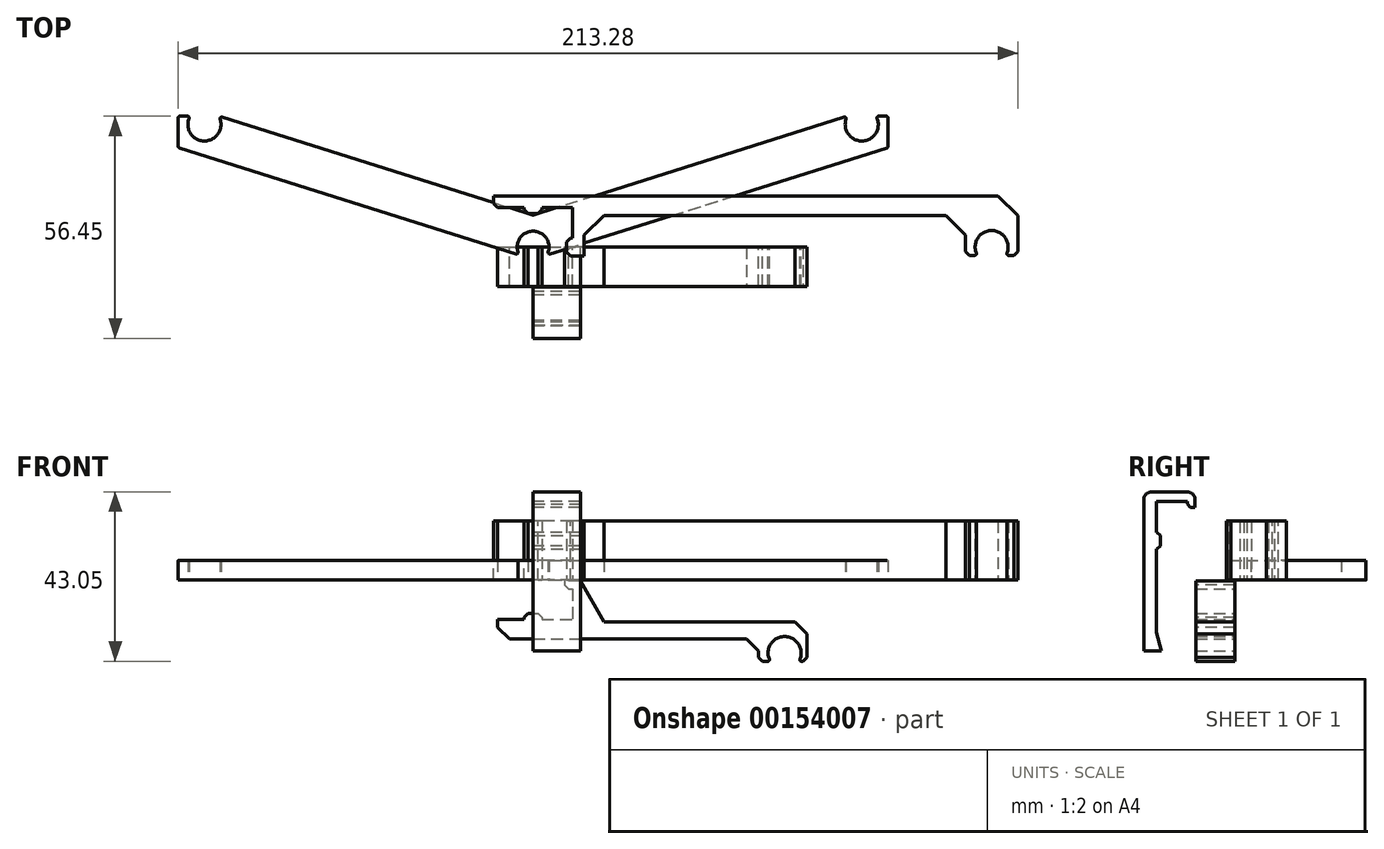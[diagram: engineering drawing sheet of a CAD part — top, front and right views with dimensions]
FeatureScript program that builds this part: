
annotation { "Feature Type Name" : "Feature", "Feature Type Description" : "" }
export const myFeature = defineFeature(function(context is Context, id is Id, definition is map)
    precondition{}
    {
        {
            var Q0;
            Q0=qCreatedBy(makeId("Front.planeOp"),FACE);
            var sketch = newSketch(context, id + "F0", { "sketchPlane" : qUnion([Q0])});
            skLineSegment(sketch, "E0.bottom", {"start": v(9, 10) * mm, "end": v(-9, 10) * mm});
            skLineSegment(sketch, "E0.top", {"start": v(9, -10) * mm, "end": v(-9, -10) * mm});
            skLineSegment(sketch, "E0.left", {"start": v(10, 9) * mm, "end": v(10, -9) * mm});
            skLineSegment(sketch, "E0.right", {"start": v(-10, 9) * mm, "end": v(-10, -9) * mm});
            skPoint(sketch, "E0.middle", {"position": v(0, 0) * mm});
            skPoint(sketch, "E1.visualSharp", {"position": v(10, 10) * mm});
            skArc(sketch, "E1.filletArc", {"start": v(10, 9) * mm, "mid": v(9.7, 9.7) * mm, "end": v(9, 10) * mm});
            skPoint(sketch, "E2.visualSharp", {"position": v(10, -10) * mm});
            skArc(sketch, "E2.filletArc", {"start": v(9, -10) * mm, "mid": v(9.7, -9.7) * mm, "end": v(10, -9) * mm});
            skPoint(sketch, "E3.visualSharp", {"position": v(-10, 10) * mm});
            skArc(sketch, "E3.filletArc", {"start": v(-9, 10) * mm, "mid": v(-9.7, 9.7) * mm, "end": v(-10, 9) * mm});
            skPoint(sketch, "E4.visualSharp", {"position": v(-10, -10) * mm});
            skArc(sketch, "E4.filletArc", {"start": v(-10, -9) * mm, "mid": v(-9.7, -9.7) * mm, "end": v(-9, -10) * mm});
            skLineSegment(sketch, "E5", {"start": v(10, 2.25) * mm, "end": v(8.5, 2.25) * mm});
            skLineSegment(sketch, "E6", {"start": v(8.5, 2.25) * mm, "end": v(8.5, 3.75) * mm});
            skLineSegment(sketch, "E7", {"start": v(8.5, 3.75) * mm, "end": v(4.45, 3.75) * mm});
            skLineSegment(sketch, "E8", {"start": v(10, -2.25) * mm, "end": v(8.5, -2.25) * mm});
            skLineSegment(sketch, "E9", {"start": v(8.5, -2.25) * mm, "end": v(8.5, -3.75) * mm});
            skLineSegment(sketch, "E10", {"start": v(8.5, -3.75) * mm, "end": v(4.45, -3.75) * mm});
            skArc(sketch, "E11", {"start": v(4.45, 3.75) * mm, "mid": v(3.3, 0) * mm, "end": v(4.45, -3.75) * mm});
            skLineSegment(sketch, "E12.1.0", {"start": v(-3.75, 8.5) * mm, "end": v(-3.75, 4.45) * mm});
            skArc(sketch, "E12.1.1", {"start": v(-3.75, 4.45) * mm, "mid": v(0, 3.3) * mm, "end": v(3.75, 4.45) * mm});
            skLineSegment(sketch, "E12.1.2", {"start": v(3.75, 8.5) * mm, "end": v(3.75, 4.45) * mm});
            skLineSegment(sketch, "E12.1.3", {"start": v(2.25, 8.5) * mm, "end": v(3.75, 8.5) * mm});
            skLineSegment(sketch, "E12.1.4", {"start": v(2.25, 10) * mm, "end": v(2.25, 8.5) * mm});
            skLineSegment(sketch, "E12.1.5", {"start": v(-2.25, 10) * mm, "end": v(-2.25, 8.5) * mm});
            skLineSegment(sketch, "E12.1.6", {"start": v(-2.25, 8.5) * mm, "end": v(-3.75, 8.5) * mm});
            skLineSegment(sketch, "E12.2.0", {"start": v(-8.5, -3.75) * mm, "end": v(-4.45, -3.75) * mm});
            skArc(sketch, "E12.2.1", {"start": v(-4.45, -3.75) * mm, "mid": v(-3.3, 0) * mm, "end": v(-4.45, 3.75) * mm});
            skLineSegment(sketch, "E12.2.2", {"start": v(-8.5, 3.75) * mm, "end": v(-4.45, 3.75) * mm});
            skLineSegment(sketch, "E12.2.3", {"start": v(-8.5, 2.25) * mm, "end": v(-8.5, 3.75) * mm});
            skLineSegment(sketch, "E12.2.4", {"start": v(-10, 2.25) * mm, "end": v(-8.5, 2.25) * mm});
            skLineSegment(sketch, "E12.2.5", {"start": v(-10, -2.25) * mm, "end": v(-8.5, -2.25) * mm});
            skLineSegment(sketch, "E12.2.6", {"start": v(-8.5, -2.25) * mm, "end": v(-8.5, -3.75) * mm});
            skLineSegment(sketch, "E12.3.0", {"start": v(3.75, -8.5) * mm, "end": v(3.75, -4.45) * mm});
            skArc(sketch, "E12.3.1", {"start": v(3.75, -4.45) * mm, "mid": v(0, -3.3) * mm, "end": v(-3.75, -4.45) * mm});
            skLineSegment(sketch, "E12.3.2", {"start": v(-3.75, -8.5) * mm, "end": v(-3.75, -4.45) * mm});
            skLineSegment(sketch, "E12.3.3", {"start": v(-2.25, -8.5) * mm, "end": v(-3.75, -8.5) * mm});
            skLineSegment(sketch, "E12.3.4", {"start": v(-2.25, -10) * mm, "end": v(-2.25, -8.5) * mm});
            skLineSegment(sketch, "E12.3.5", {"start": v(2.25, -10) * mm, "end": v(2.25, -8.5) * mm});
            skLineSegment(sketch, "E12.3.6", {"start": v(2.25, -8.5) * mm, "end": v(3.75, -8.5) * mm});
            skSolve(sketch);
        }
        {
            var Q0;
            Q0=qCreatedBy(makeId("Front.planeOp"),FACE);
            var sketch = newSketch(context, id + "F1", { "sketchPlane" : qUnion([Q0])});
            skLineSegment(sketch, "E13.0", {"start": v(10, -2.25) * mm, "end": v(8.5, -2.25) * mm, "construction": true});
            skLineSegment(sketch, "E14.0", {"start": v(10, 9) * mm, "end": v(10, -9) * mm, "construction": true});
            skLineSegment(sketch, "E15.0", {"start": v(9, -10) * mm, "end": v(-9, -10) * mm, "construction": true});
            skLineSegment(sketch, "E16.0", {"start": v(2.25, -10) * mm, "end": v(2.25, -8.5) * mm, "construction": true});
            skLineSegment(sketch, "E17.0", {"start": v(-2.25, -10) * mm, "end": v(-2.25, -8.5) * mm, "construction": true});
            skLineSegment(sketch, "E18", {"start": v(8, -2.25) * mm, "end": v(10, -2.25) * mm});
            skLineSegment(sketch, "E19", {"start": v(10, -2.25) * mm, "end": v(10, -10) * mm});
            skCircle(sketch, "E20", {"center": v(63.9, -18.55) * mm, "radius": 4.2 * mm});
            skLineSegment(sketch, "E21", {"start": v(-9, -10) * mm, "end": v(-9, -20.65) * mm});
            skLineSegment(sketch, "E22", {"start": v(-9, -20.65) * mm, "end": v(60.26, -20.65) * mm});
            skLineSegment(sketch, "E23", {"start": v(67.54, -20.65) * mm, "end": v(69.54, -20.65) * mm});
            skLineSegment(sketch, "E24", {"start": v(69.54, -20.65) * mm, "end": v(69.54, -10.65) * mm});
            skLineSegment(sketch, "E25", {"start": v(69.54, -10.65) * mm, "end": v(18, -10.65) * mm});
            skLineSegment(sketch, "E26", {"start": v(18, -10.65) * mm, "end": v(12, -0.25) * mm});
            skLineSegment(sketch, "E27", {"start": v(12, -0.25) * mm, "end": v(8, -0.25) * mm});
            skLineSegment(sketch, "E28", {"start": v(8, -0.25) * mm, "end": v(8, -2.25) * mm});
            skLineSegment(sketch, "E29", {"start": v(-9, -15) * mm, "end": v(57.26, -15) * mm});
            skLineSegment(sketch, "E30", {"start": v(57.26, -15) * mm, "end": v(57.26, -20.65) * mm});
            skLineSegment(sketch, "E31", {"start": v(63.9, -18.55) * mm, "end": v(60.26, -20.65) * mm, "construction": true});
            skLineSegment(sketch, "E32", {"start": v(63.9, -18.55) * mm, "end": v(67.54, -20.65) * mm, "construction": true});
            skLineSegment(sketch, "E33", {"start": v(59.7, -18.55) * mm, "end": v(68.1, -18.55) * mm, "construction": true});
            skLineSegment(sketch, "E34", {"start": v(-9, -10) * mm, "end": v(-2.25, -10) * mm});
            skLineSegment(sketch, "E35", {"start": v(-2.25, -10) * mm, "end": v(-2.25, -8.5) * mm});
            skLineSegment(sketch, "E36", {"start": v(-2.25, -8.5) * mm, "end": v(2.25, -8.5) * mm});
            skLineSegment(sketch, "E37", {"start": v(2.25, -8.5) * mm, "end": v(2.25, -10) * mm});
            skLineSegment(sketch, "E38", {"start": v(2.25, -10) * mm, "end": v(10, -10) * mm});
            skSolve(sketch);
        }
        {
            var Q0;
            Q0=makeQuery(id+"F1.imprint","IMPRINT",FACE,{"disambiguationData":[TD([[makeQuery(id+"F1.imprint","IMPRINT",EDGE,{"derivedFrom":sQuery(id+"F1.wireOp",EDGE,"E18")}),1.0]])]});
            extrude(context, id + "F2", {"entities" : qUnion([Q0]), "depth" : 10 * mm});
        }
        {
            var Q0;
            Q0=makeQuery(id+"F2.opExtrude","SWEPT_EDGE",EDGE,{"disambiguationData":[OSD([sQuery(id+"F1.wireOp",EDGE,"E35"),sQuery(id+"F1.wireOp",EDGE,"E36")])]});
            var Q1;
            Q1=makeQuery(id+"F2.opExtrude","SWEPT_EDGE",EDGE,{"disambiguationData":[OSD([sQuery(id+"F1.wireOp",EDGE,"E36"),sQuery(id+"F1.wireOp",EDGE,"E37")])]});
            var Q2;
            Q2=makeQuery(id+"F2.opExtrude","SWEPT_EDGE",EDGE,{"disambiguationData":[OSD([sQuery(id+"F1.wireOp",EDGE,"E18"),sQuery(id+"F1.wireOp",EDGE,"E28")])]});
            var Q3;
            Q3=makeQuery(id+"F2.opExtrude","SWEPT_EDGE",EDGE,{"disambiguationData":[OSD([sQuery(id+"F1.wireOp",EDGE,"E22"),sQuery(id+"F1.wireOp",EDGE,"E30")])]});
            var Q4;
            Q4=makeQuery(id+"F2.opExtrude","SWEPT_EDGE",EDGE,{"disambiguationData":[OSD([sQuery(id+"F1.wireOp",EDGE,"E23"),sQuery(id+"F1.wireOp",EDGE,"E24")])]});
            chamfer(context, id + "F3", {"entities" : qUnion([Q0, Q1, Q2, Q3, Q4]), "width" : 1 * mm, "tangentPropagation" : true});
        }
        {
            var Q0;
            Q0=makeQuery(id+"F2.opExtrude","SWEPT_EDGE",EDGE,{"disambiguationData":[OSD([sQuery(id+"F1.wireOp",EDGE,"E21"),sQuery(id+"F1.wireOp",EDGE,"E29")])]});
            var Q1;
            Q1=makeQuery(id+"F2.opExtrude","SWEPT_EDGE",EDGE,{"disambiguationData":[OSD([sQuery(id+"F1.wireOp",EDGE,"E29"),sQuery(id+"F1.wireOp",EDGE,"E30")])]});
            var Q2;
            Q2=makeQuery(id+"F2.opExtrude","SWEPT_EDGE",EDGE,{"disambiguationData":[OSD([sQuery(id+"F1.wireOp",EDGE,"E24"),sQuery(id+"F1.wireOp",EDGE,"E25")])]});
            chamfer(context, id + "F4", {"entities" : qUnion([Q0, Q1, Q2]), "width" : 3 * mm, "tangentPropagation" : true});
        }
        {
            var Q0;
            Q0=qCreatedBy(makeId("Top.planeOp"),FACE);
            var sketch = newSketch(context, id + "F5", { "sketchPlane" : qUnion([Q0])});
            skLineSegment(sketch, "E39.bottom", {"start": v(10, 10) * mm, "end": v(-10, 10) * mm, "construction": true});
            skLineSegment(sketch, "E39.top", {"start": v(10, -10) * mm, "end": v(-10, -10) * mm, "construction": true});
            skLineSegment(sketch, "E39.left", {"start": v(10, 10) * mm, "end": v(10, -10) * mm, "construction": true});
            skLineSegment(sketch, "E39.right", {"start": v(-10, 10) * mm, "end": v(-10, -10) * mm, "construction": true});
            skPoint(sketch, "E39.middle", {"position": v(0, 0) * mm});
            skCircle(sketch, "E40", {"center": v(116.5, 0) * mm, "radius": 4.2 * mm});
            skLineSegment(sketch, "E41", {"start": v(-10, 10) * mm, "end": v(-10, 13) * mm});
            skLineSegment(sketch, "E42", {"start": v(-10, 13) * mm, "end": v(123.14, 13) * mm});
            skLineSegment(sketch, "E43", {"start": v(123.14, 13) * mm, "end": v(123.14, -2.1) * mm});
            skLineSegment(sketch, "E44", {"start": v(123.14, -2.1) * mm, "end": v(120.14, -2.1) * mm});
            skLineSegment(sketch, "E45", {"start": v(112.86, -2.1) * mm, "end": v(109.86, -2.1) * mm});
            skLineSegment(sketch, "E46", {"start": v(109.86, -2.1) * mm, "end": v(109.86, 8) * mm});
            skLineSegment(sketch, "E47", {"start": v(109.86, 8) * mm, "end": v(13, 8) * mm});
            skLineSegment(sketch, "E48", {"start": v(13, 8) * mm, "end": v(13, -2.25) * mm});
            skLineSegment(sketch, "E49", {"start": v(13, -2.25) * mm, "end": v(10, -2.25) * mm});
            skLineSegment(sketch, "E50", {"start": v(10, -2.25) * mm, "end": v(8.5, -2.25) * mm});
            skLineSegment(sketch, "E51", {"start": v(8.5, -2.25) * mm, "end": v(8.5, 2.25) * mm});
            skLineSegment(sketch, "E52", {"start": v(8.5, 2.25) * mm, "end": v(10, 2.25) * mm});
            skLineSegment(sketch, "E53", {"start": v(10, 2.25) * mm, "end": v(10, 10) * mm});
            skLineSegment(sketch, "E54", {"start": v(10, 10) * mm, "end": v(2.25, 10) * mm});
            skLineSegment(sketch, "E55", {"start": v(2.25, 10) * mm, "end": v(2.25, 8.5) * mm});
            skLineSegment(sketch, "E56", {"start": v(2.25, 8.5) * mm, "end": v(-2.25, 8.5) * mm});
            skLineSegment(sketch, "E57", {"start": v(-2.25, 8.5) * mm, "end": v(-2.25, 10) * mm});
            skLineSegment(sketch, "E58", {"start": v(-2.25, 10) * mm, "end": v(-10, 10) * mm});
            skLineSegment(sketch, "E59", {"start": v(112.3, 0) * mm, "end": v(120.7, 0) * mm, "construction": true});
            skLineSegment(sketch, "E60", {"start": v(116.5, 0) * mm, "end": v(112.86, -2.1) * mm, "construction": true});
            skLineSegment(sketch, "E61", {"start": v(116.5, 0) * mm, "end": v(120.14, -2.1) * mm, "construction": true});
            skSolve(sketch);
        }
        {
            var Q0;
            Q0=makeQuery(id+"F5.imprint","IMPRINT",FACE,{"disambiguationData":[TD([[makeQuery(id+"F5.imprint","IMPRINT",EDGE,{"derivedFrom":sQuery(id+"F5.wireOp",EDGE,"E41")}),-1.0]])]});
            extrude(context, id + "F6", {"entities" : qUnion([Q0]), "depth" : 15 * mm});
        }
        {
            var Q0;
            Q0=makeQuery(id+"F6.opExtrude","SWEPT_EDGE",EDGE,{"disambiguationData":[OSD([sQuery(id+"F5.wireOp",EDGE,"E51"),sQuery(id+"F5.wireOp",EDGE,"E52")])]});
            var Q1;
            Q1=makeQuery(id+"F6.opExtrude","SWEPT_EDGE",EDGE,{"disambiguationData":[OSD([sQuery(id+"F5.wireOp",EDGE,"E50"),sQuery(id+"F5.wireOp",EDGE,"E51")])]});
            var Q2;
            Q2=makeQuery(id+"F6.opExtrude","SWEPT_EDGE",EDGE,{"disambiguationData":[OSD([sQuery(id+"F5.wireOp",EDGE,"E56"),sQuery(id+"F5.wireOp",EDGE,"E57")])]});
            var Q3;
            Q3=makeQuery(id+"F6.opExtrude","SWEPT_EDGE",EDGE,{"disambiguationData":[OSD([sQuery(id+"F5.wireOp",EDGE,"E55"),sQuery(id+"F5.wireOp",EDGE,"E56")])]});
            var Q4;
            Q4=makeQuery(id+"F6.opExtrude","SWEPT_EDGE",EDGE,{"disambiguationData":[OSD([sQuery(id+"F5.wireOp",EDGE,"E41"),sQuery(id+"F5.wireOp",EDGE,"E58")])]});
            var Q5;
            Q5=makeQuery(id+"F6.opExtrude","SWEPT_EDGE",EDGE,{"disambiguationData":[OSD([sQuery(id+"F5.wireOp",EDGE,"E45"),sQuery(id+"F5.wireOp",EDGE,"E46")])]});
            var Q6;
            Q6=makeQuery(id+"F6.opExtrude","SWEPT_EDGE",EDGE,{"disambiguationData":[OSD([sQuery(id+"F5.wireOp",EDGE,"E43"),sQuery(id+"F5.wireOp",EDGE,"E44")])]});
            chamfer(context, id + "F7", {"entities" : qUnion([Q0, Q1, Q2, Q3, Q4, Q5, Q6]), "width" : 1 * mm, "tangentPropagation" : true});
        }
        {
            var Q0;
            Q0=makeQuery(id+"F6.opExtrude","SWEPT_EDGE",EDGE,{"disambiguationData":[OSD([sQuery(id+"F5.wireOp",EDGE,"E42"),sQuery(id+"F5.wireOp",EDGE,"E43")])]});
            var Q1;
            Q1=makeQuery(id+"F6.opExtrude","SWEPT_EDGE",EDGE,{"disambiguationData":[OSD([sQuery(id+"F5.wireOp",EDGE,"E46"),sQuery(id+"F5.wireOp",EDGE,"E47")])]});
            var Q2;
            Q2=makeQuery(id+"F6.opExtrude","SWEPT_EDGE",EDGE,{"disambiguationData":[OSD([sQuery(id+"F5.wireOp",EDGE,"E47"),sQuery(id+"F5.wireOp",EDGE,"E48")])]});
            chamfer(context, id + "F8", {"entities" : qUnion([Q0, Q1, Q2]), "width" : 5 * mm, "tangentPropagation" : true});
        }
        {
            var Q0;
            Q0=makeQuery(id+"F2.opExtrude","SWEPT_EDGE",EDGE,{"disambiguationData":[OSD([sQuery(id+"F1.wireOp",EDGE,"E20"),sQuery(id+"F1.wireOp",EDGE,"E22")])]});
            var Q1;
            Q1=makeQuery(id+"F2.opExtrude","SWEPT_EDGE",EDGE,{"disambiguationData":[OSD([sQuery(id+"F1.wireOp",EDGE,"E20"),sQuery(id+"F1.wireOp",EDGE,"E23")])]});
            var Q2;
            Q2=makeQuery(id+"F6.opExtrude","SWEPT_EDGE",EDGE,{"disambiguationData":[OSD([sQuery(id+"F5.wireOp",EDGE,"E40"),sQuery(id+"F5.wireOp",EDGE,"E45")])]});
            var Q3;
            Q3=makeQuery(id+"F6.opExtrude","SWEPT_EDGE",EDGE,{"disambiguationData":[OSD([sQuery(id+"F5.wireOp",EDGE,"E40"),sQuery(id+"F5.wireOp",EDGE,"E44")])]});
            fillet(context, id + "F9", {"entities" : qUnion([Q0, Q1, Q2, Q3]), "radius" : 0.4 * mm, "tangentPropagation" : true, "allowEdgeOverflow" : false});
        }
        {
            var Q0;
            Q0=qCreatedBy(makeId("Top.planeOp"),FACE);
            var sketch = newSketch(context, id + "F10", { "sketchPlane" : qUnion([Q0])});
            skCircle(sketch, "E62", {"center": v(0, 0) * mm, "radius": 4.05 * mm});
            skCircle(sketch, "E63", {"center": v(-83.5, 31.15) * mm, "radius": 4.2 * mm});
            skLineSegment(sketch, "E64", {"start": v(0, 0) * mm, "end": v(0, 66.48) * mm, "construction": true});
            skCircle(sketch, "E65.MirrorC", {"center": v(83.5, 31.15) * mm, "radius": 4.2 * mm});
            skLineSegment(sketch, "E66", {"start": v(-79.3, 31.15) * mm, "end": v(-87.7, 31.15) * mm, "construction": true});
            skLineSegment(sketch, "E67", {"start": v(-4.05, 0) * mm, "end": v(4.05, 0) * mm, "construction": true});
            skLineSegment(sketch, "E68", {"start": v(-83.5, 31.15) * mm, "end": v(-87.14, 33.25) * mm, "construction": true});
            skLineSegment(sketch, "E69", {"start": v(-83.5, 31.15) * mm, "end": v(-79.86, 33.25) * mm, "construction": true});
            skLineSegment(sketch, "E70", {"start": v(0, 0) * mm, "end": v(-3.5, -2.02) * mm, "construction": true});
            skLineSegment(sketch, "E71", {"start": v(0, 0) * mm, "end": v(3.5, -2.02) * mm, "construction": true});
            skLineSegment(sketch, "E72", {"start": v(-87.14, 33.25) * mm, "end": v(-90.14, 33.25) * mm});
            skLineSegment(sketch, "E73", {"start": v(-90.14, 33.25) * mm, "end": v(-90.14, 25.25) * mm});
            skLineSegment(sketch, "E74", {"start": v(-90.14, 25.25) * mm, "end": v(-90.14, 25.25) * mm});
            skLineSegment(sketch, "E75", {"start": v(-3.5, -2.03) * mm, "end": v(-90.14, 25.25) * mm});
            skLineSegment(sketch, "E76", {"start": v(-79.86, 33.25) * mm, "end": v(0, 8.1) * mm});
            skLineSegment(sketch, "E77.MirrorCS", {"start": v(79.86, 33.25) * mm, "end": v(0, 8.1) * mm});
            skLineSegment(sketch, "E78.MirrorCS", {"start": v(3.5, -2.03) * mm, "end": v(90.14, 25.25) * mm});
            skLineSegment(sketch, "E79.MirrorCS", {"start": v(90.14, 33.25) * mm, "end": v(90.14, 25.25) * mm});
            skLineSegment(sketch, "E80.MirrorCS", {"start": v(83.5, 31.15) * mm, "end": v(79.86, 33.25) * mm, "construction": true});
            skLineSegment(sketch, "E81.MirrorCS", {"start": v(83.5, 31.15) * mm, "end": v(87.14, 33.25) * mm, "construction": true});
            skLineSegment(sketch, "E82.MirrorCS", {"start": v(87.14, 33.25) * mm, "end": v(90.14, 33.25) * mm});
            skSolve(sketch);
        }
        {
            var Q0;
            {var subQ5=sQuery(id+"F10.wireOp",EDGE,"E72");Q0=makeQuery(id+"F10.imprint","IMPRINT",FACE,{"disambiguationData":[TD([[makeQuery(id+"F10.imprint","IMPRINT",EDGE,{"derivedFrom":subQ5}),1.0]])]});}
            extrude(context, id + "F15", {"entities" : qUnion([Q0]), "depth" : 5 * mm});
        }
        {
            var Q0;
            Q0=makeQuery(id+"F15.opExtrude","SWEPT_EDGE",EDGE,{"disambiguationData":[OSD([sQuery(id+"F10.wireOp",EDGE,"E62"),sQuery(id+"F10.wireOp",EDGE,"E75")])]});
            var Q1;
            Q1=makeQuery(id+"F15.opExtrude","SWEPT_EDGE",EDGE,{"disambiguationData":[OSD([sQuery(id+"F10.wireOp",EDGE,"E62"),sQuery(id+"F10.wireOp",EDGE,"E78.MirrorCS")])]});
            var Q2;
            Q2=makeQuery(id+"F15.opExtrude","SWEPT_EDGE",EDGE,{"disambiguationData":[OSD([sQuery(id+"F10.wireOp",EDGE,"E76"),sQuery(id+"F10.wireOp",EDGE,"E77.MirrorCS")])]});
            var Q3;
            Q3=makeQuery(id+"F15.opExtrude","SWEPT_EDGE",EDGE,{"disambiguationData":[OSD([sQuery(id+"F10.wireOp",EDGE,"E65.MirrorC"),sQuery(id+"F10.wireOp",EDGE,"E77.MirrorCS")])]});
            var Q4;
            Q4=makeQuery(id+"F15.opExtrude","SWEPT_EDGE",EDGE,{"disambiguationData":[OSD([sQuery(id+"F10.wireOp",EDGE,"E65.MirrorC"),sQuery(id+"F10.wireOp",EDGE,"E82.MirrorCS")])]});
            var Q5;
            Q5=makeQuery(id+"F15.opExtrude","SWEPT_EDGE",EDGE,{"disambiguationData":[OSD([sQuery(id+"F10.wireOp",EDGE,"E79.MirrorCS"),sQuery(id+"F10.wireOp",EDGE,"E82.MirrorCS")])]});
            var Q6;
            Q6=makeQuery(id+"F15.opExtrude","SWEPT_EDGE",EDGE,{"disambiguationData":[OSD([sQuery(id+"F10.wireOp",EDGE,"E78.MirrorCS"),sQuery(id+"F10.wireOp",EDGE,"E79.MirrorCS")])]});
            var Q7;
            Q7=makeQuery(id+"F15.opExtrude","SWEPT_EDGE",EDGE,{"disambiguationData":[OSD([sQuery(id+"F10.wireOp",EDGE,"E72"),sQuery(id+"F10.wireOp",EDGE,"E73")])]});
            var Q8;
            Q8=makeQuery(id+"F15.opExtrude","SWEPT_EDGE",EDGE,{"disambiguationData":[OSD([sQuery(id+"F10.wireOp",EDGE,"E73"),sQuery(id+"F10.wireOp",EDGE,"E75")])]});
            var Q9;
            Q9=makeQuery(id+"F15.opExtrude","SWEPT_EDGE",EDGE,{"disambiguationData":[OSD([sQuery(id+"F10.wireOp",EDGE,"E63"),sQuery(id+"F10.wireOp",EDGE,"E76")])]});
            var Q10;
            Q10=makeQuery(id+"F15.opExtrude","SWEPT_EDGE",EDGE,{"disambiguationData":[OSD([sQuery(id+"F10.wireOp",EDGE,"E63"),sQuery(id+"F10.wireOp",EDGE,"E72")])]});
            fillet(context, id + "F16", {"entities" : qUnion([Q0, Q1, Q2, Q3, Q4, Q5, Q6, Q7, Q8, Q9, Q10]), "radius" : 0.4 * mm, "tangentPropagation" : true, "allowEdgeOverflow" : false});
        }
        {
            var Q0;
            Q0=qCreatedBy(makeId("Right.planeOp"),FACE);
            var sketch = newSketch(context, id + "F11", { "sketchPlane" : qUnion([Q0])});
            skLineSegment(sketch, "E83.bottom", {"start": v(0, 0) * mm, "end": v(-20, 0) * mm, "construction": true});
            skLineSegment(sketch, "E83.top", {"start": v(0, 20) * mm, "end": v(-20, 20) * mm, "construction": true});
            skLineSegment(sketch, "E83.left", {"start": v(0, 0) * mm, "end": v(0, 20) * mm, "construction": true});
            skLineSegment(sketch, "E83.right", {"start": v(-20, 0) * mm, "end": v(-20, 20) * mm, "construction": true});
            skLineSegment(sketch, "E84", {"start": v(-12.15, 18.5) * mm, "end": v(-12.15, 20) * mm});
            skLineSegment(sketch, "E85", {"start": v(-12.15, 20) * mm, "end": v(-20, 20) * mm});
            skLineSegment(sketch, "E86", {"start": v(-20, 12.15) * mm, "end": v(-19, 12.15) * mm});
            skLineSegment(sketch, "E87", {"start": v(-19, 12.15) * mm, "end": v(-19, 7.85) * mm});
            skLineSegment(sketch, "E88", {"start": v(-19, 7.85) * mm, "end": v(-20, 7.85) * mm});
            skLineSegment(sketch, "E89", {"start": v(-20, 7.85) * mm, "end": v(-20, -13) * mm});
            skLineSegment(sketch, "E90", {"start": v(-18.66, -18) * mm, "end": v(-23.2, -18) * mm});
            skLineSegment(sketch, "E91", {"start": v(-23.2, -18) * mm, "end": v(-23.2, 22.4) * mm});
            skLineSegment(sketch, "E92", {"start": v(-23.2, 22.4) * mm, "end": v(-10.15, 22.4) * mm});
            skLineSegment(sketch, "E93", {"start": v(-10.15, 22.4) * mm, "end": v(-10.15, 18.5) * mm});
            skLineSegment(sketch, "E94", {"start": v(-10.15, 18.5) * mm, "end": v(-12.15, 18.5) * mm});
            skLineSegment(sketch, "E95", {"start": v(-20, -13) * mm, "end": v(-18.66, -18) * mm});
            skLineSegment(sketch, "E96", {"start": v(-20, 20) * mm, "end": v(-20, 12.15) * mm});
            skSolve(sketch);
        }
        {
            var Q0;
            Q0=makeQuery(id+"F11.imprint","IMPRINT",FACE,{"disambiguationData":[TD([[makeQuery(id+"F11.imprint","IMPRINT",EDGE,{"derivedFrom":sQuery(id+"F11.wireOp",EDGE,"E84")}),-1.0]])]});
            extrude(context, id + "F12", {"entities" : qUnion([Q0]), "depth" : 12 * mm});
        }
        {
            var Q0;
            Q0=makeQuery(id+"F12.opExtrude","SWEPT_EDGE",EDGE,{"disambiguationData":[OSD([sQuery(id+"F11.wireOp",EDGE,"E86"),sQuery(id+"F11.wireOp",EDGE,"E87")])]});
            var Q1;
            Q1=makeQuery(id+"F12.opExtrude","SWEPT_EDGE",EDGE,{"disambiguationData":[OSD([sQuery(id+"F11.wireOp",EDGE,"E84"),sQuery(id+"F11.wireOp",EDGE,"E94")])]});
            var Q2;
            Q2=makeQuery(id+"F12.opExtrude","SWEPT_EDGE",EDGE,{"disambiguationData":[OSD([sQuery(id+"F11.wireOp",EDGE,"E87"),sQuery(id+"F11.wireOp",EDGE,"E88")])]});
            chamfer(context, id + "F13", {"entities" : qUnion([Q0, Q1, Q2]), "width" : 0.8 * mm, "tangentPropagation" : true});
        }
        {
            var Q0;
            Q0=makeQuery(id+"F12.opExtrude","SWEPT_EDGE",EDGE,{"disambiguationData":[OSD([sQuery(id+"F11.wireOp",EDGE,"E91"),sQuery(id+"F11.wireOp",EDGE,"E92")])]});
            var Q1;
            Q1=makeQuery(id+"F12.opExtrude","SWEPT_EDGE",EDGE,{"disambiguationData":[OSD([sQuery(id+"F11.wireOp",EDGE,"E89"),sQuery(id+"F11.wireOp",EDGE,"E95")])]});
            var Q2;
            Q2=makeQuery(id+"F12.opExtrude","SWEPT_EDGE",EDGE,{"disambiguationData":[OSD([sQuery(id+"F11.wireOp",EDGE,"E92"),sQuery(id+"F11.wireOp",EDGE,"E93")])]});
            fillet(context, id + "F14", {"entities" : qUnion([Q0, Q1, Q2]), "radius" : 2 * mm, "tangentPropagation" : true, "allowEdgeOverflow" : false});
        }
    });
